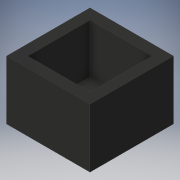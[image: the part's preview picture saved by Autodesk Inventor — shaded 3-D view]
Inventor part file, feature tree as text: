
AUTODESK INVENTOR PART (.ipt)
format: ipt  version: 2019 (Build 230136000, 136)  size: 109,568 bytes
history: native  units: mm
features: extrude x2, sketch x2
ambient origin geometry x8: Origin, YZ Plane, XZ Plane, XY Plane, X Axis, Y Axis, Z Axis, Center Point
bodies: Solid1 (feature_tree)
feature tree (4):
  extrude  "Extrusion1"  Depth=17.0mm
  extrude  "Extrusion2"  Depth=12.7mm
  sketch  "Sketch1"  dims[d0=17.0mm d1=17.0mm]
  sketch  "Sketch2"  dims[d2=2.0mm d3=0.0mm d4=12.7mm d5=10.0mm d6=0.0mm]
